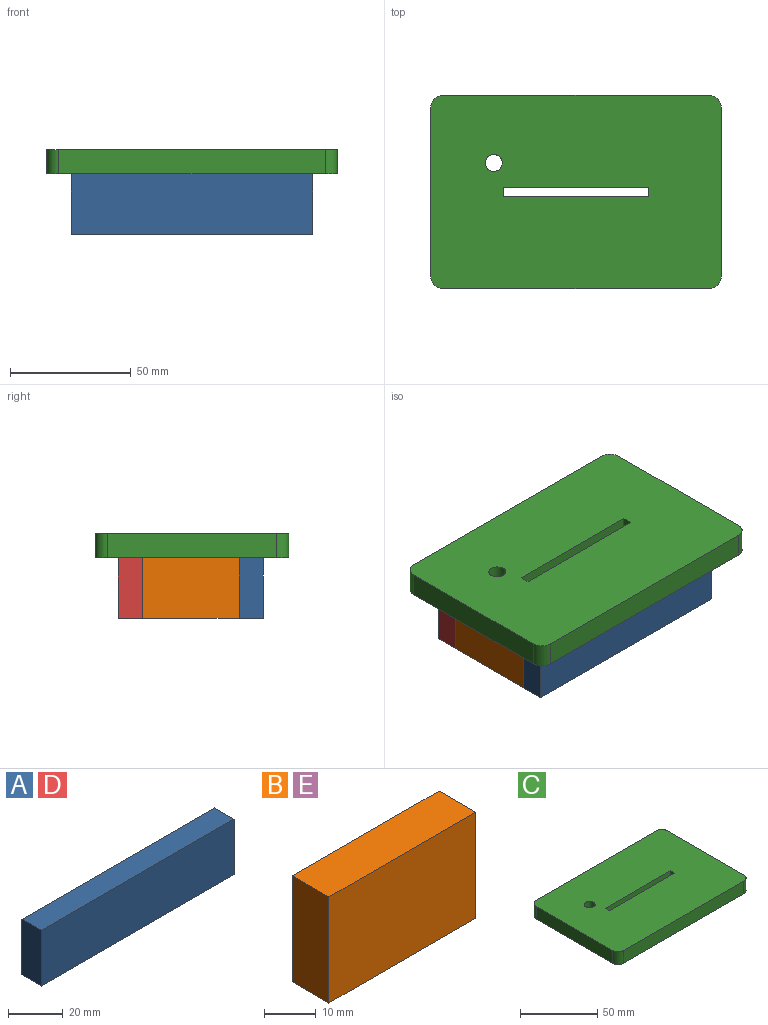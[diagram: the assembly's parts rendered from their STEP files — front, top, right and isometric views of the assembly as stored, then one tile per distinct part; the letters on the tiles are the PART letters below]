
ASSEMBLY  parts=5 mates=3
PART A: 6 faces, bbox 100x10x25 mm
  f0: plane 100x10mm, normal (0,0,1), area 1000mm2, adj f1,f3,f4,f5
  f1: plane 25x10mm, normal (-1,0,0), area 250mm2, adj f0,f2,f4,f5
  f2: plane 100x10mm, normal (0,0,-1), area 1000mm2, adj f1,f3,f4,f5
  f3: plane 25x10mm, normal (1,0,0), area 250mm2, adj f0,f2,f4,f5
  f4: plane 100x25mm, normal (0,-1,0), area 2500mm2, adj f0,f1,f2,f3
  f5: plane 100x25mm, normal (0,1,0), area 2500mm2, adj f0,f1,f2,f3
PART B: 6 faces, bbox 40x10x25 mm
  f0: plane 40x10mm, normal (0,0,1), area 400mm2, adj f1,f3,f4,f5
  f1: plane 25x10mm, normal (-1,0,0), area 250mm2, adj f0,f2,f4,f5
  f2: plane 40x10mm, normal (0,0,-1), area 400mm2, adj f1,f3,f4,f5
  f3: plane 25x10mm, normal (1,0,0), area 250mm2, adj f0,f2,f4,f5
  f4: plane 40x25mm, normal (0,-1,0), area 1000mm2, adj f0,f1,f2,f3
  f5: plane 40x25mm, normal (0,1,0), area 1000mm2, adj f0,f1,f2,f3
PART C: 15 faces, bbox 120x80x10 mm
  f0: plane 70x10mm, normal (-1,0,0), area 700mm2, adj f1,f12,f13,f14
  f1: cylinder r=5mm len=10mm, axis (0,0,-1), area 78.5mm2, adj f0,f2,f13,f14
  f2: plane 110x10mm, normal (0,-1,0), area 1100mm2, adj f1,f3,f13,f14
  f3: cylinder r=5mm len=10mm, axis (0,0,-1), area 78.5mm2, adj f2,f4,f13,f14
  f4: plane 70x10mm, normal (1,0,0), area 700mm2, adj f3,f5,f13,f14
  f5: cylinder r=5mm len=10mm, axis (0,0,-1), area 78.5mm2, adj f4,f6,f13,f14
  f6: plane 110x10mm, normal (0,1,0), area 1100mm2, adj f5,f12,f13,f14
  f7: plane 10x4mm, normal (1,0,0), area 40mm2, adj f8,f11,f13,f14
  f8: plane 60x10mm, normal (0,-1,0), area 600mm2, adj f7,f9,f13,f14
  f9: plane 10x4mm, normal (-1,0,0), area 40mm2, adj f8,f11,f13,f14
  f10: cylinder r=3.5mm len=10mm, axis (0,0,-1), area 219.9mm2, adj f13,f14
  f11: plane 60x10mm, normal (0,1,0), area 600mm2, adj f7,f9,f13,f14
  f12: cylinder r=5mm len=10mm, axis (0,0,-1), area 78.5mm2, adj f0,f6,f13,f14
  f13: plane 120x80mm, normal (0,0,1), area 9300.1mm2, adj f0,f1,f2,f3,f4,f5,f6,f7
  f14: plane 120x80mm, normal (0,0,-1), area 9300.1mm2, adj f0,f1,f2,f3,f4,f5,f6,f7
PART D: same geometry as A
PART E: same geometry as B
PLACE A rot(axis=(1,0,0),0deg) t=(-34,10,0)mm
PLACE B rot(axis=(-0.71,0.71,0),180deg) t=(-80.33,2.95,4.67)mm
PLACE C rot(axis=(1,0,0),0deg) t=(-52.53,19.38,8.61)mm
PLACE D rot(axis=(0,-1,0),180deg) t=(-26.66,60,-7.78)mm
PLACE E rot(axis=(-0.71,0.71,0),180deg) t=(9.67,2.95,4.67)mm
MATE parallel B.f3 <-> A.f5  axis (0,-1,0) through (-80.33,10,-3.89)mm
MATE parallel D.f4 <-> E.f1  axis (0,-1,0) through (19.67,50,-3.89)mm
MATE fastened C.f14 <-> E.f2  axis (0,0,-1) through (-30.33,31.5,8.61)mm
